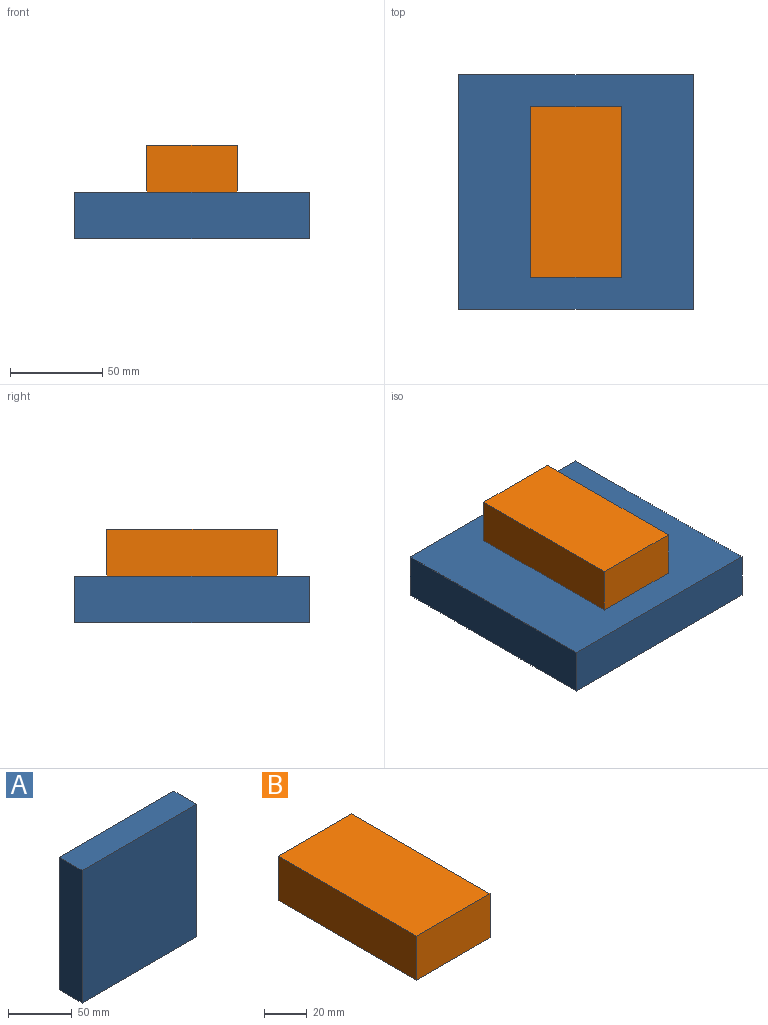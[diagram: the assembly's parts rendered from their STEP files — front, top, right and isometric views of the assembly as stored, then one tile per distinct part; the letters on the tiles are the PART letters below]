
ASSEMBLY  parts=2 mates=1
PART A: 6 faces, bbox 127x25.4x127 mm
  f0: plane 127x25.4mm, normal (1,0,0), area 3225.8mm2, adj f1,f3,f4,f5
  f1: plane 127x25.4mm, normal (0,0,1), area 3225.8mm2, adj f0,f2,f4,f5
  f2: plane 127x25.4mm, normal (-1,0,0), area 3225.8mm2, adj f1,f3,f4,f5
  f3: plane 127x25.4mm, normal (0,0,-1), area 3225.8mm2, adj f0,f2,f4,f5
  f4: plane 127x127mm, normal (0,-1,0), area 16129mm2, adj f0,f1,f2,f3
  f5: plane 127x127mm, normal (0,1,0), area 16129mm2, adj f0,f1,f2,f3
PART B: 6 faces, bbox 48.9x92.2x25.4 mm
  f0: plane 92.23x25.4mm, normal (1,0,0), area 2342.5mm2, adj f1,f3,f4,f5
  f1: plane 48.86x25.4mm, normal (0,1,0), area 1241.1mm2, adj f0,f2,f4,f5
  f2: plane 92.23x25.4mm, normal (-1,0,0), area 2342.5mm2, adj f1,f3,f4,f5
  f3: plane 48.86x25.4mm, normal (0,-1,0), area 1241.1mm2, adj f0,f2,f4,f5
  f4: plane 92.23x48.86mm, normal (0,0,1), area 4506.2mm2, adj f0,f1,f2,f3
  f5: plane 92.23x48.86mm, normal (0,0,-1), area 4506.2mm2, adj f0,f1,f2,f3
PLACE A rot(axis=(-0.58,0.58,-0.58),120deg) t=(10.69,0,-25.4)mm
PLACE B at identity
MATE slider A.f4 <-> B.f5  axis (0,0,1) through (10.69,0,0)mm
